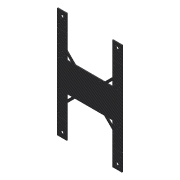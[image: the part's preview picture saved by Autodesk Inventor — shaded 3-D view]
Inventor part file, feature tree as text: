
AUTODESK INVENTOR PART (.ipt)
format: ipt  version: 2018 (Build 220112000, 112)  size: 264,704 bytes
history: native  units: mm
features: other x5, plane x2, mirror x2, sketch x1, extrude x1, reference x1
ambient origin geometry x8: Origin, YZ Plane, XZ Plane, XY Plane, X Axis, Y Axis, Z Axis, Center Point
bodies: Volumenkörper1 (feature_tree)
feature tree (12):
  sketch  "Skizze1"  dims[d10=100.0mm d12=30.0mm d13=170.0mm d14=45.0mm d15=3.0mm d16=0.0mm d17=0.0mm d18=0.0mm d22=5.0mm d23=4.0mm d26=3.4mm d59=30.0mm d60=8.0mm d61=15.0mm d64=3.4mm d65=3.4mm d66=3.4mm d67=3.4mm d70=7.802084mm d74=16.0mm d75=19.0mm d76=90.0deg d78=0.5mm d79=52.0mm d82=3.4mm d83=3.4mm d84=7.0mm d85=7.0mm d88=15.0mm d89=10.0mm d90=3.4mm d91=3.4mm d92=16.0mm d94=3.4mm d95=15.0mm]
  extrude  "Extrusion1"  Depth=30.0mm
  plane  "Arbeitsebene1"
  plane  "Arbeitsebene2"
  mirror  "Spiegeln1"
  other  "Arbeitsachse1"
  mirror  "Spiegeln2"
  reference  "Referenz1"
  other  "<userpath>\OneDrive\Development\Mohne\03_Konstruktion\Mohne komplett.iam"
  other  "Mohne komplett.iam"
  other  "EMax Motor:1"
  other  "01000A-040-002-LE_6"
